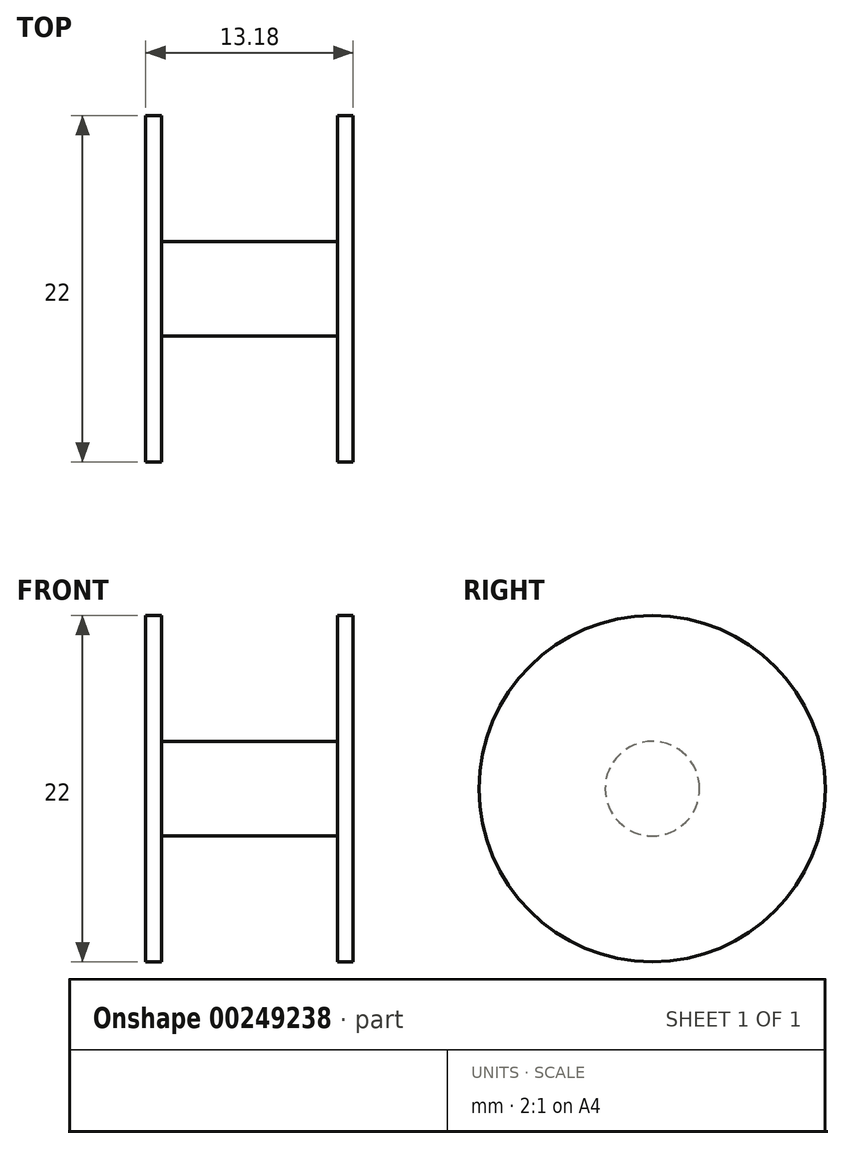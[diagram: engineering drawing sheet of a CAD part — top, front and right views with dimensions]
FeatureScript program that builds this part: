
annotation { "Feature Type Name" : "Feature", "Feature Type Description" : "" }
export const myFeature = defineFeature(function(context is Context, id is Id, definition is map)
    precondition{}
    {
        {
            var Q0;
            Q0=qCreatedBy(makeId("Top.planeOp"),FACE);
            var sketch = newSketch(context, id + "F0", { "sketchPlane" : qUnion([Q0])});
            skLineSegment(sketch, "E0", {"start": v(-0.51, 3) * mm, "end": v(-11.69, 3) * mm});
            skLineSegment(sketch, "E1", {"start": v(-11.69, 3) * mm, "end": v(-11.69, 11) * mm});
            skLineSegment(sketch, "E2", {"start": v(-11.69, 11) * mm, "end": v(-12.69, 11) * mm});
            skLineSegment(sketch, "E3", {"start": v(-12.69, 11) * mm, "end": v(-12.69, 0) * mm});
            skLineSegment(sketch, "E4", {"start": v(-12.69, 0) * mm, "end": v(0.49, 0) * mm});
            skLineSegment(sketch, "E5", {"start": v(0.49, 0) * mm, "end": v(0.49, 11) * mm});
            skLineSegment(sketch, "E6", {"start": v(0.49, 11) * mm, "end": v(-0.51, 11) * mm});
            skLineSegment(sketch, "E7", {"start": v(-0.51, 11) * mm, "end": v(-0.51, 3) * mm});
            skSolve(sketch);
        }
        {
            var Q0;
            Q0 = qSketchRegion(id + "F0", true);
            var Q1;
            Q1=sQuery(id+"F0.wireOp",EDGE,"E4");
            revolve(context, id + "F1", {"entities" : qUnion([Q0]), "axis" : qUnion([Q1]), "revolveType" : RevolveType.FULL});
        }
    });
